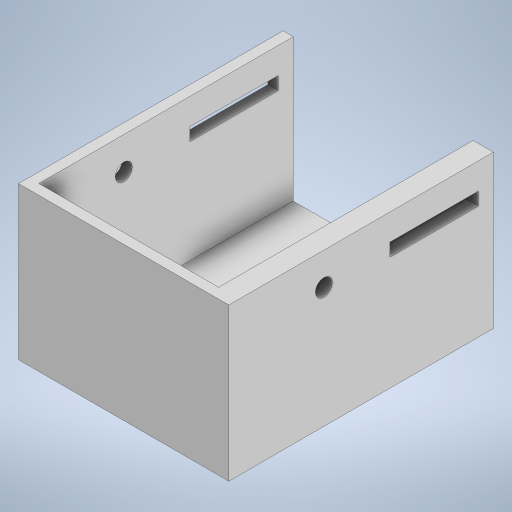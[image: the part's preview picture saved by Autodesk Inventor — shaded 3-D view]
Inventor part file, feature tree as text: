
AUTODESK INVENTOR PART (.ipt)
format: ipt  version: 2023 (Build 270158000, 158)  size: 233,984 bytes
history: native  units: in
note: dims shown in document units (in); Inventor stores cm internally (conversion verified against a paired STEP export)
features: sketch x6, extrude x5, shell x1
ambient origin geometry x8: Origin, YZ Plane, XZ Plane, XY Plane, X Axis, Y Axis, Z Axis, Center Point
bodies: Solid1 (feature_tree)
feature tree (12):
  extrude  "Extrusion1"  Depth=3.0709in
  shell  "Shell1"  Thickness=1.7717in
  sketch  "Sketch4"  dims[d4=0.1181in d17=0.3937in d18=0.0in]
  extrude  "Extrusion3"  Depth=0.3937in TaperAngle=0.0deg
  sketch  "Sketch6"  dims[d21=0.1772in d22=1.3189in]
  extrude  "Extrusion5"  Depth=0.1496in
  extrude  "Extrusion6"  Depth=1.3189in
  extrude  "Extrusion7"  TaperAngle=0.0deg  [1 undecoded]
  sketch  "Sketch2"  dims[d0=2.3228in d1=3.0709in d2=1.7717in d3=0.0in]
  sketch  "Sketch5"  dims[d19=1.0236in d20=0.1496in]
  sketch  "Sketch7"  dims[d25=0.1181in d26=0.0in d27=0.0in d28=0.0in]
  sketch  "Sketch8"  dims[d29=0.1969in d30=0.0in d31=0.0in d13=0.0197in d14=0.0344in d15=0.0197in d16=0.0344in]
note: 1 required parameter value undecoded (feature->parameter linkage not recoverable at this tier; creation-order binding heuristic only, values carry confidence <= 0.55)
